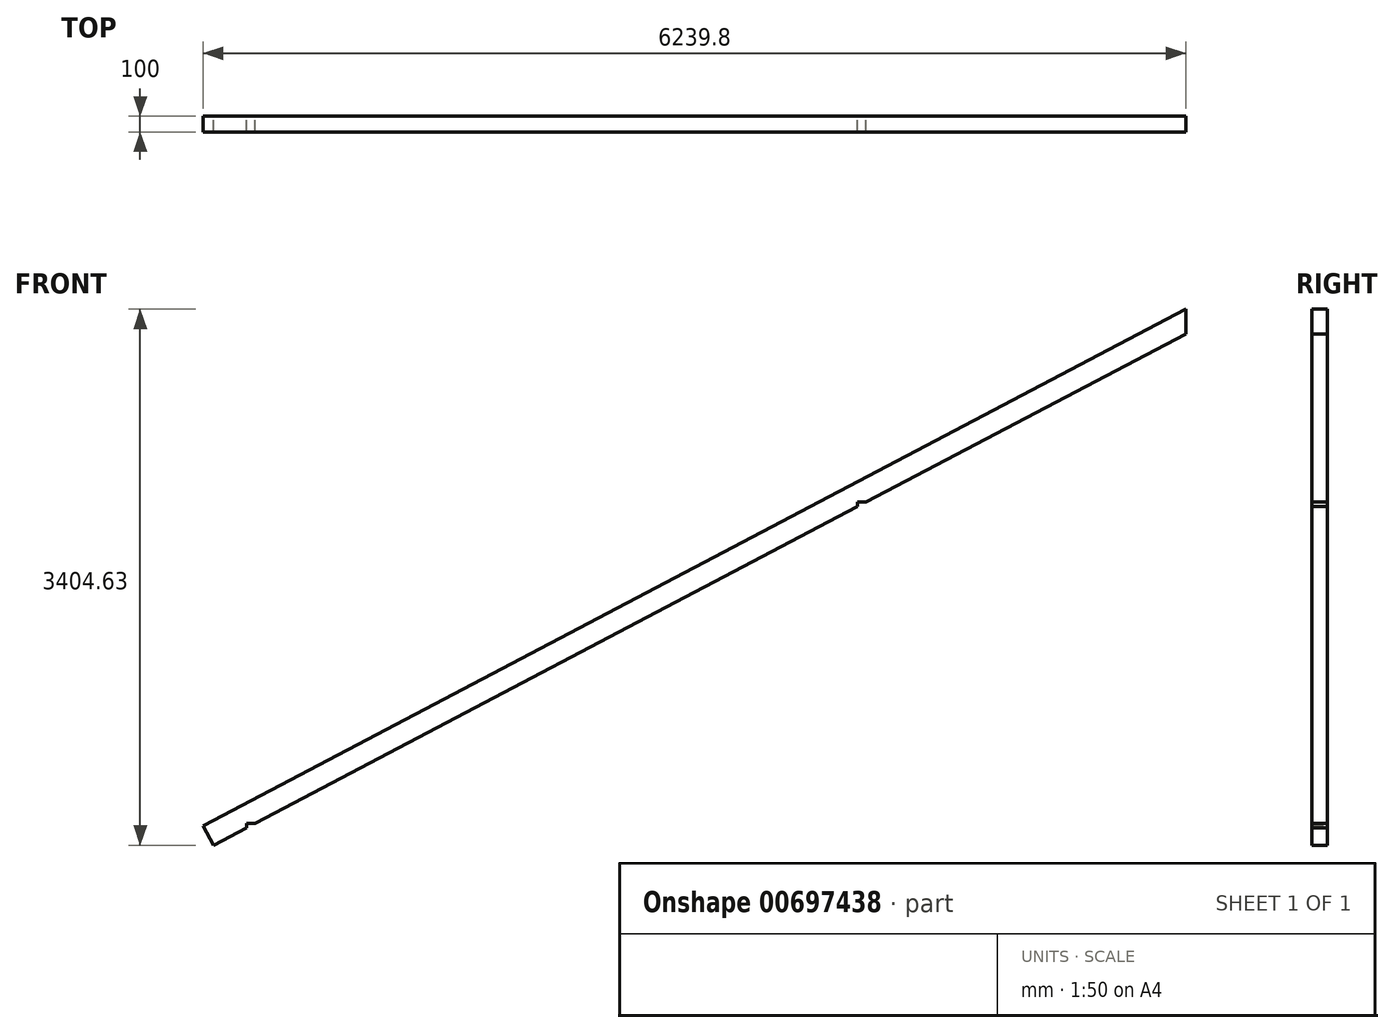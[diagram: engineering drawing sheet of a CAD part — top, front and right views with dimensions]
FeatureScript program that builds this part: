
annotation { "Feature Type Name" : "Feature", "Feature Type Description" : "" }
export const myFeature = defineFeature(function(context is Context, id is Id, definition is map)
    precondition{}
    {
        {
            var Q0;
            Q0=qCreatedBy(makeId("Front.planeOp"),FACE);
            var sketch = newSketch(context, id + "F0", { "sketchPlane" : qUnion([Q0])});
            skLineSegment(sketch, "E0", {"start": v(-2689.83, -1428.69) * mm, "end": v(-2754.99, -1304.77) * mm});
            skLineSegment(sketch, "E1", {"start": v(-2754.99, -1304.77) * mm, "end": v(3484.81, 1975.94) * mm});
            skLineSegment(sketch, "E2", {"start": v(3484.81, 1817.77) * mm, "end": v(3484.81, 1975.94) * mm});
            skLineSegment(sketch, "E3", {"start": v(3484.81, 1817.77) * mm, "end": v(1453.53, 749.78) * mm});
            skLineSegment(sketch, "E4", {"start": v(1453.53, 749.78) * mm, "end": v(1399.81, 749.78) * mm});
            skLineSegment(sketch, "E5", {"start": v(1399.81, 721.54) * mm, "end": v(-2426.47, -1290.22) * mm});
            skLineSegment(sketch, "E6", {"start": v(-2426.47, -1290.22) * mm, "end": v(-2480.19, -1290.22) * mm});
            skLineSegment(sketch, "E7", {"start": v(-2480.19, -1318.46) * mm, "end": v(-2689.83, -1428.69) * mm});
            skLineSegment(sketch, "E8", {"start": v(-2480.19, -1290.22) * mm, "end": v(-2480.19, -1318.46) * mm});
            skLineSegment(sketch, "E9", {"start": v(1399.81, 749.78) * mm, "end": v(1399.81, 721.54) * mm});
            skSolve(sketch);
        }
        {
            var Q0;
            Q0=makeQuery(id+"F0.imprint","IMPRINT",FACE,{"disambiguationData":[TD([[makeQuery(id+"F0.imprint","IMPRINT",EDGE,{"derivedFrom":sQuery(id+"F0.wireOp",EDGE,"E0")}),-1.0]])]});
            extrude(context, id + "F1", {"entities" : qUnion([Q0]), "depth" : 100 * mm, "offsetDistance" : 25 * mm});
        }
    });
